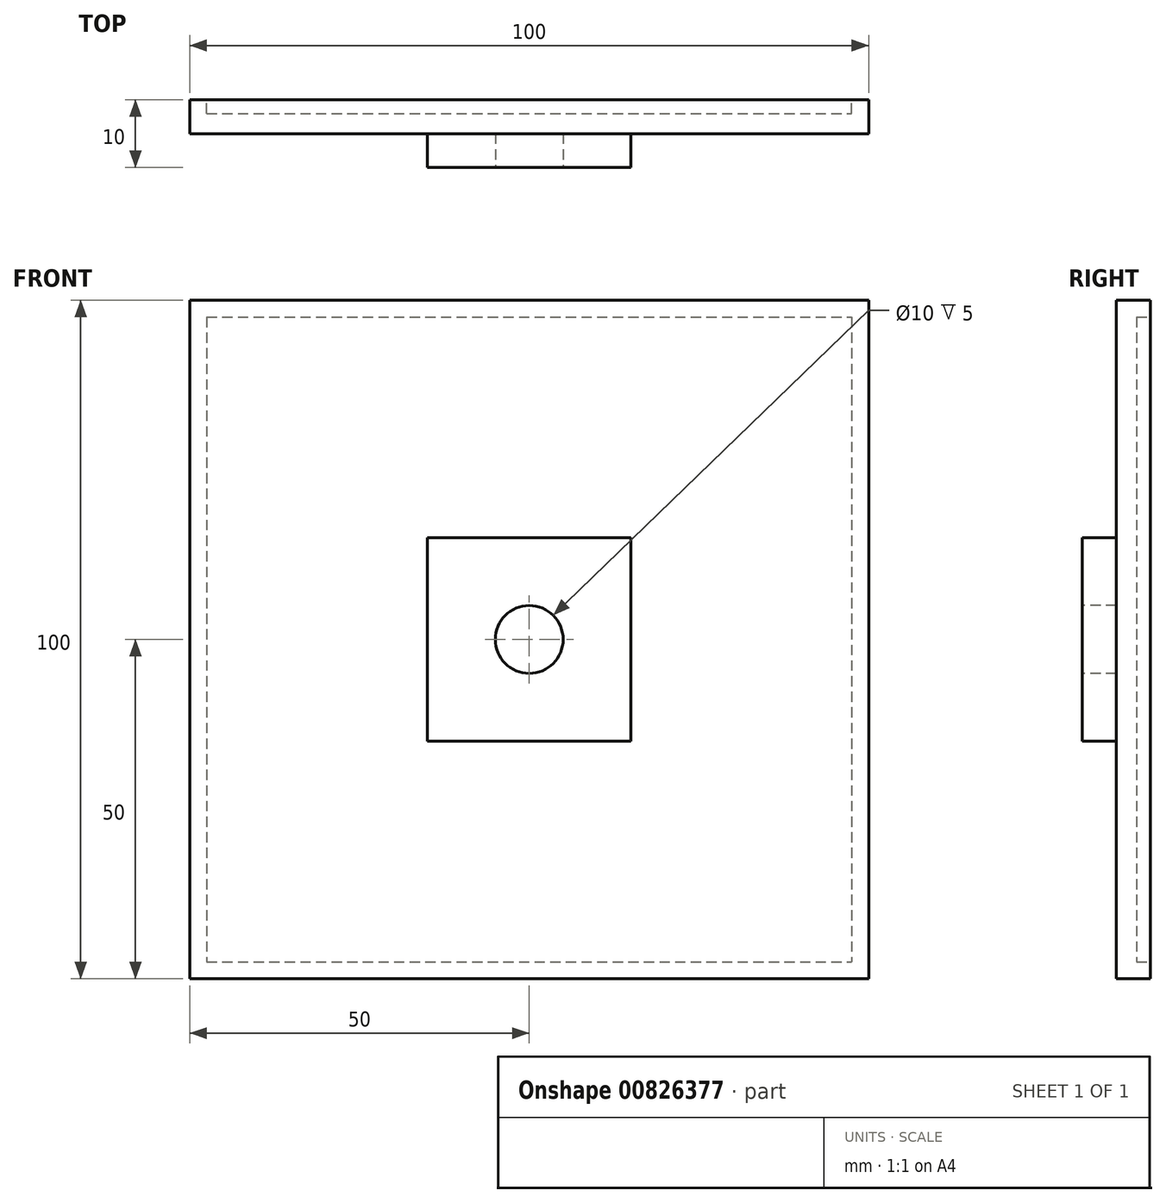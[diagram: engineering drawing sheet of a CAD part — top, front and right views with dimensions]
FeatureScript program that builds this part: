
annotation { "Feature Type Name" : "Feature", "Feature Type Description" : "" }
export const myFeature = defineFeature(function(context is Context, id is Id, definition is map)
    precondition{}
    {
        {
            var Q0;
            Q0=qCreatedBy(makeId("Front.planeOp"),FACE);
            var sketch = newSketch(context, id + "F0", { "sketchPlane" : qUnion([Q0])});
            skLineSegment(sketch, "E0.bottom", {"start": v(-50, 50) * mm, "end": v(50, 50) * mm});
            skLineSegment(sketch, "E0.top", {"start": v(-50, -50) * mm, "end": v(50, -50) * mm});
            skLineSegment(sketch, "E0.left", {"start": v(-50, 50) * mm, "end": v(-50, -50) * mm});
            skLineSegment(sketch, "E0.right", {"start": v(50, 50) * mm, "end": v(50, -50) * mm});
            skLineSegment(sketch, "E1.bottom", {"start": v(-47.5, 47.5) * mm, "end": v(47.5, 47.5) * mm});
            skLineSegment(sketch, "E1.top", {"start": v(-47.5, -47.5) * mm, "end": v(47.5, -47.5) * mm});
            skLineSegment(sketch, "E1.left", {"start": v(-47.5, 47.5) * mm, "end": v(-47.5, -47.5) * mm});
            skLineSegment(sketch, "E1.right", {"start": v(47.5, 47.5) * mm, "end": v(47.5, -47.5) * mm});
            skSolve(sketch);
        }
        {
            var Q0;
            Q0=makeQuery(id+"F0.imprint","IMPRINT",FACE,{"disambiguationData":[TD([[makeQuery(id+"F0.imprint","IMPRINT",EDGE,{"derivedFrom":sQuery(id+"F0.wireOp",EDGE,"E1.bottom")}),-1.0]])]});
            var Q1;
            Q1=makeQuery(id+"F0.imprint","IMPRINT",FACE,{"disambiguationData":[TD([[makeQuery(id+"F0.imprint","IMPRINT",EDGE,{"derivedFrom":sQuery(id+"F0.wireOp",EDGE,"E0.bottom")}),-1.0]])]});
            extrude(context, id + "F1", {"entities" : qUnion([Q0, Q1]), "depth" : 5 * mm, "offsetDistance" : 25 * mm});
        }
        {
            var Q0;
            Q0=makeQuery(id+"F0.imprint","IMPRINT",FACE,{"disambiguationData":[TD([[makeQuery(id+"F0.imprint","IMPRINT",EDGE,{"derivedFrom":sQuery(id+"F0.wireOp",EDGE,"E1.bottom")}),-1.0]])]});
            extrude(context, id + "F2", {"entities" : qUnion([Q0]), "operationType" : NewBodyOperationType.REMOVE, "depth" : 2 * mm, "offsetDistance" : 25 * mm});
        }
        {
            var Q0;
            Q0=makeQuery(id+"F1.opExtrude","CAP_FACE",FACE,{"disambiguationData":[OSD([sQuery(id+"F0.wireOp",EDGE,"E0.bottom"),sQuery(id+"F0.wireOp",EDGE,"E0.top"),sQuery(id+"F0.wireOp",EDGE,"E0.left"),sQuery(id+"F0.wireOp",EDGE,"E0.right")])],"isStart":false});
            var sketch = newSketch(context, id + "F3", { "sketchPlane" : qUnion([Q0])});
            skLineSegment(sketch, "E2.bottom", {"start": v(-15, 15) * mm, "end": v(15, 15) * mm});
            skLineSegment(sketch, "E2.top", {"start": v(-15, -15) * mm, "end": v(15, -15) * mm});
            skLineSegment(sketch, "E2.left", {"start": v(-15, 15) * mm, "end": v(-15, -15) * mm});
            skLineSegment(sketch, "E2.right", {"start": v(15, 15) * mm, "end": v(15, -15) * mm});
            skSolve(sketch);
        }
        {
            var Q0;
            Q0=makeQuery(id+"F3.imprint","IMPRINT",FACE,{"disambiguationData":[TD([[makeQuery(id+"F3.imprint","IMPRINT",EDGE,{"derivedFrom":sQuery(id+"F3.wireOp",EDGE,"E2.bottom")}),-1.0]])]});
            extrude(context, id + "F4", {"entities" : qUnion([Q0]), "operationType" : NewBodyOperationType.ADD, "depth" : 5 * mm, "offsetDistance" : 25 * mm});
        }
        {
            var Q0;
            Q0=makeQuery(id+"F4.opExtrude","CAP_FACE",FACE,{"disambiguationData":[OSD([sQuery(id+"F3.wireOp",EDGE,"E2.bottom"),sQuery(id+"F3.wireOp",EDGE,"E2.top"),sQuery(id+"F3.wireOp",EDGE,"E2.left"),sQuery(id+"F3.wireOp",EDGE,"E2.right")])],"isStart":false});
            var sketch = newSketch(context, id + "F5", { "sketchPlane" : qUnion([Q0])});
            skCircle(sketch, "E3", {"center": v(0, 0) * mm, "radius": 5 * mm});
            skSolve(sketch);
        }
        {
            var Q0;
            Q0=makeQuery(id+"F5.imprint","IMPRINT",FACE,{"disambiguationData":[TD([[makeQuery(id+"F5.imprint","IMPRINT",EDGE,{"derivedFrom":sQuery(id+"F5.wireOp",EDGE,"E3")}),1.0]])]});
            extrude(context, id + "F6", {"entities" : qUnion([Q0]), "operationType" : NewBodyOperationType.REMOVE, "oppositeDirection" : true, "depth" : 5 * mm, "offsetDistance" : 25 * mm});
        }
    });
